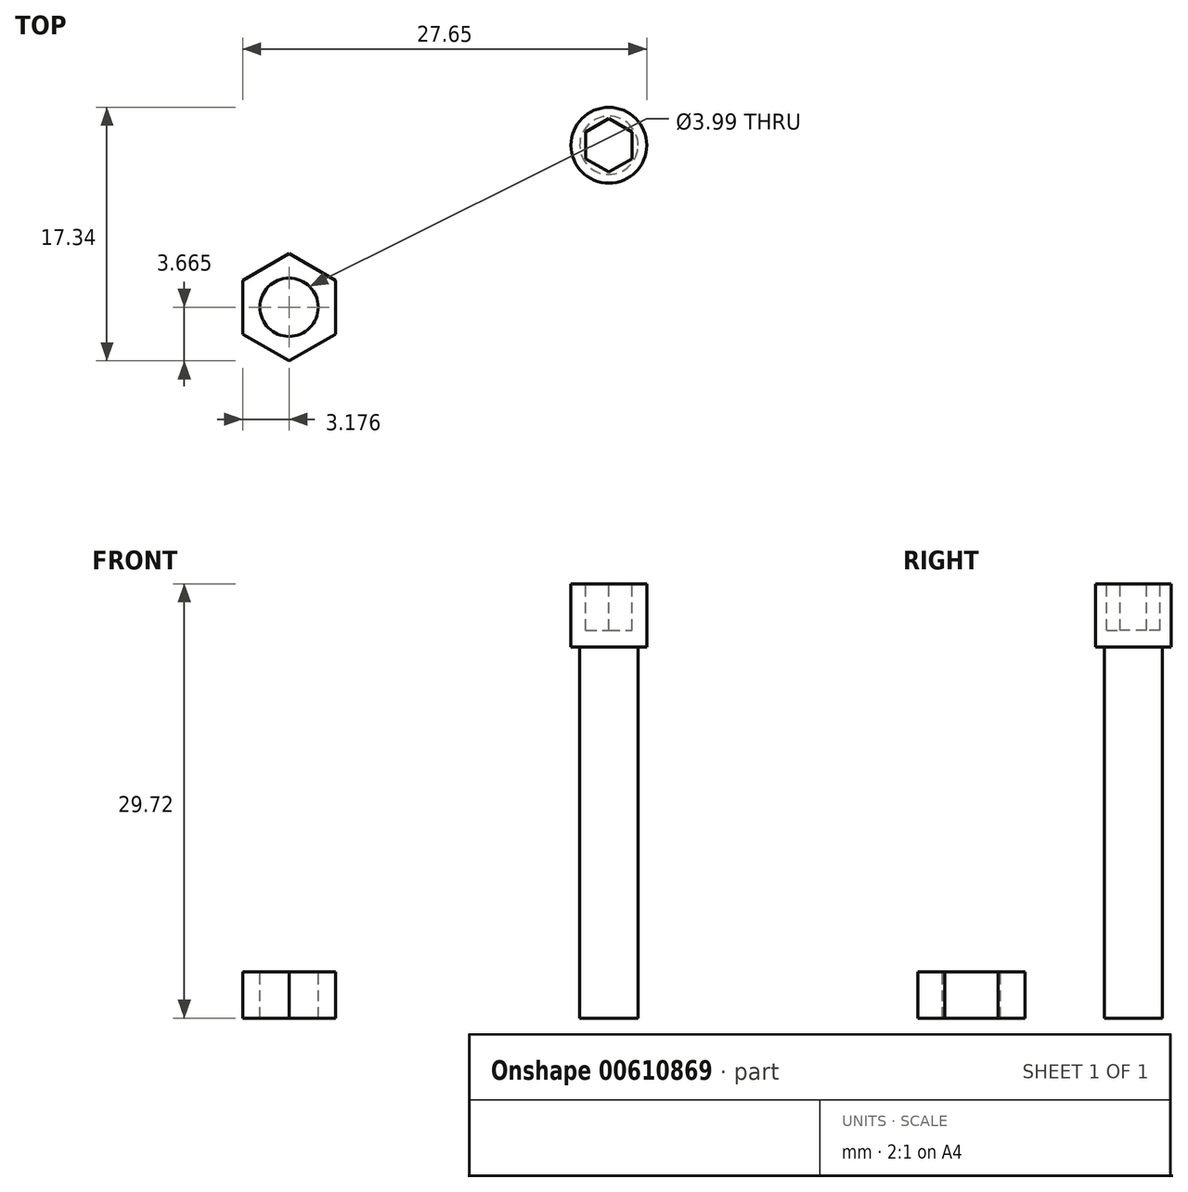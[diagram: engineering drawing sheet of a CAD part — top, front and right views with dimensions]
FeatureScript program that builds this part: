
annotation { "Feature Type Name" : "Feature", "Feature Type Description" : "" }
export const myFeature = defineFeature(function(context is Context, id is Id, definition is map)
    precondition{}
    {
        {
            var Q0;
            Q0=qCreatedBy(makeId("Top.planeOp"),FACE);
            var sketch = newSketch(context, id + "F0", { "sketchPlane" : qUnion([Q0])});
            skCircle(sketch, "E0", {"center": v(0, 0) * mm, "radius": 2 * mm});
            skSolve(sketch);
        }
        {
            var Q0;
            Q0=makeQuery(id+"F0.imprint","IMPRINT",FACE,{"disambiguationData":[TD([[makeQuery(id+"F0.imprint","IMPRINT",EDGE,{"derivedFrom":sQuery(id+"F0.wireOp",EDGE,"E0")}),1.0]])]});
            extrude(context, id + "F1", {"entities" : qUnion([Q0]), "depth" : 25.4 * mm, "offsetDistance" : 25.4 * mm});
        }
        {
            var Q0;
            Q0=makeQuery(id+"F1.opExtrude","CAP_FACE",FACE,{"disambiguationData":[OSD([sQuery(id+"F0.wireOp",EDGE,"E0")])],"isStart":false});
            var sketch = newSketch(context, id + "F2", { "sketchPlane" : qUnion([Q0])});
            skCircle(sketch, "E1", {"center": v(0, 0) * mm, "radius": 2.6 * mm});
            skSolve(sketch);
        }
        {
            var Q0;
            Q0=makeQuery(id+"F2.imprint","IMPRINT",FACE,{"disambiguationData":[TD([[makeQuery(id+"F2.imprint","IMPRINT",EDGE,{"derivedFrom":sQuery(id+"F2.wireOp",EDGE,"E1")}),1.0]])]});
            var Q1;
            Q1=makeQuery(id+"F2.imprint","IMPRINT",FACE,{"disambiguationData":[TD([[makeQuery(id+"F2.imprint","IMPRINT",EDGE,{"derivedFrom":makeQuery(id+"F1.opExtrude","CAP_EDGE",EDGE,{"disambiguationData":[OSD([sQuery(id+"F0.wireOp",EDGE,"E0")])],"isStart":false})}),1.0]])]});
            extrude(context, id + "F3", {"entities" : qUnion([Q0, Q1]), "operationType" : NewBodyOperationType.ADD, "depth" : 4.32 * mm, "offsetDistance" : 25.4 * mm});
        }
        {
            var Q0;
            Q0=makeQuery(id+"F3.opExtrude","CAP_FACE",FACE,{"disambiguationData":[OSD([sQuery(id+"F2.wireOp",EDGE,"E1")])],"isStart":false});
            var sketch = newSketch(context, id + "F4", { "sketchPlane" : qUnion([Q0])});
            skCircle(sketch, "E2.cCircle", {"center": v(0, 0) * mm, "radius": 1.59 * mm, "construction": true});
            skLineSegment(sketch, "E2.0", {"start": v(1.59, 0.92) * mm, "end": v(1.59, -0.92) * mm});
            skLineSegment(sketch, "E2.1", {"start": v(1.59, -0.92) * mm, "end": v(0, -1.83) * mm});
            skLineSegment(sketch, "E2.2", {"start": v(0, -1.83) * mm, "end": v(-1.59, -0.92) * mm});
            skLineSegment(sketch, "E2.3", {"start": v(-1.59, -0.92) * mm, "end": v(-1.59, 0.92) * mm});
            skLineSegment(sketch, "E2.4", {"start": v(-1.59, 0.92) * mm, "end": v(0, 1.83) * mm});
            skLineSegment(sketch, "E2.5", {"start": v(0, 1.83) * mm, "end": v(1.59, 0.92) * mm});
            skPoint(sketch, "E2.0.midPoint", {"position": v(1.59, 0) * mm});
            skSolve(sketch);
        }
        {
            var Q0;
            Q0=makeQuery(id+"F4.imprint","IMPRINT",FACE,{"disambiguationData":[TD([[makeQuery(id+"F4.imprint","IMPRINT",EDGE,{"derivedFrom":sQuery(id+"F4.wireOp",EDGE,"E2.0")}),-1.0]])]});
            extrude(context, id + "F5", {"entities" : qUnion([Q0]), "operationType" : NewBodyOperationType.REMOVE, "oppositeDirection" : true, "depth" : 3.17 * mm, "offsetDistance" : 25.4 * mm});
        }
        {
            var Q0;
            Q0=qCreatedBy(makeId("Top.planeOp"),FACE);
            var sketch = newSketch(context, id + "F6", { "sketchPlane" : qUnion([Q0])});
            skCircle(sketch, "E3.cCircle", {"center": v(-21.88, -11.08) * mm, "radius": 3.18 * mm, "construction": true});
            skLineSegment(sketch, "E3.0", {"start": v(-18.7, -9.25) * mm, "end": v(-18.7, -12.92) * mm});
            skLineSegment(sketch, "E3.1", {"start": v(-18.7, -12.92) * mm, "end": v(-21.88, -14.75) * mm});
            skLineSegment(sketch, "E3.2", {"start": v(-21.88, -14.75) * mm, "end": v(-25.06, -12.92) * mm});
            skLineSegment(sketch, "E3.3", {"start": v(-25.06, -12.92) * mm, "end": v(-25.06, -9.25) * mm});
            skLineSegment(sketch, "E3.4", {"start": v(-25.06, -9.25) * mm, "end": v(-21.88, -7.42) * mm});
            skLineSegment(sketch, "E3.5", {"start": v(-21.88, -7.42) * mm, "end": v(-18.7, -9.25) * mm});
            skPoint(sketch, "E3.0.midPoint", {"position": v(-18.7, -11.08) * mm});
            skSolve(sketch);
        }
        {
            var Q0;
            Q0=makeQuery(id+"F6.imprint","IMPRINT",FACE,{"disambiguationData":[TD([[makeQuery(id+"F6.imprint","IMPRINT",EDGE,{"derivedFrom":sQuery(id+"F6.wireOp",EDGE,"E3.0")}),-1.0]])]});
            extrude(context, id + "F7", {"entities" : qUnion([Q0]), "depth" : 3.17 * mm, "offsetDistance" : 25.4 * mm});
        }
        {
            var Q0;
            Q0=makeQuery(id+"F7.opExtrude","CAP_FACE",FACE,{"disambiguationData":[OSD([sQuery(id+"F6.wireOp",EDGE,"E3.0"),sQuery(id+"F6.wireOp",EDGE,"E3.1"),sQuery(id+"F6.wireOp",EDGE,"E3.2"),sQuery(id+"F6.wireOp",EDGE,"E3.3"),sQuery(id+"F6.wireOp",EDGE,"E3.4"),sQuery(id+"F6.wireOp",EDGE,"E3.5")])],"isStart":false});
            var sketch = newSketch(context, id + "F8", { "sketchPlane" : qUnion([Q0])});
            skCircle(sketch, "E4", {"center": v(-21.88, -11.08) * mm, "radius": 2 * mm});
            skSolve(sketch);
        }
        {
            var Q0;
            Q0=makeQuery(id+"F8.imprint","IMPRINT",FACE,{"disambiguationData":[TD([[makeQuery(id+"F8.imprint","IMPRINT",EDGE,{"derivedFrom":sQuery(id+"F8.wireOp",EDGE,"E4")}),1.0]])]});
            extrude(context, id + "F9", {"entities" : qUnion([Q0]), "operationType" : NewBodyOperationType.REMOVE, "oppositeDirection" : true, "depth" : 6.35 * mm, "offsetDistance" : 25.4 * mm});
        }
    });
